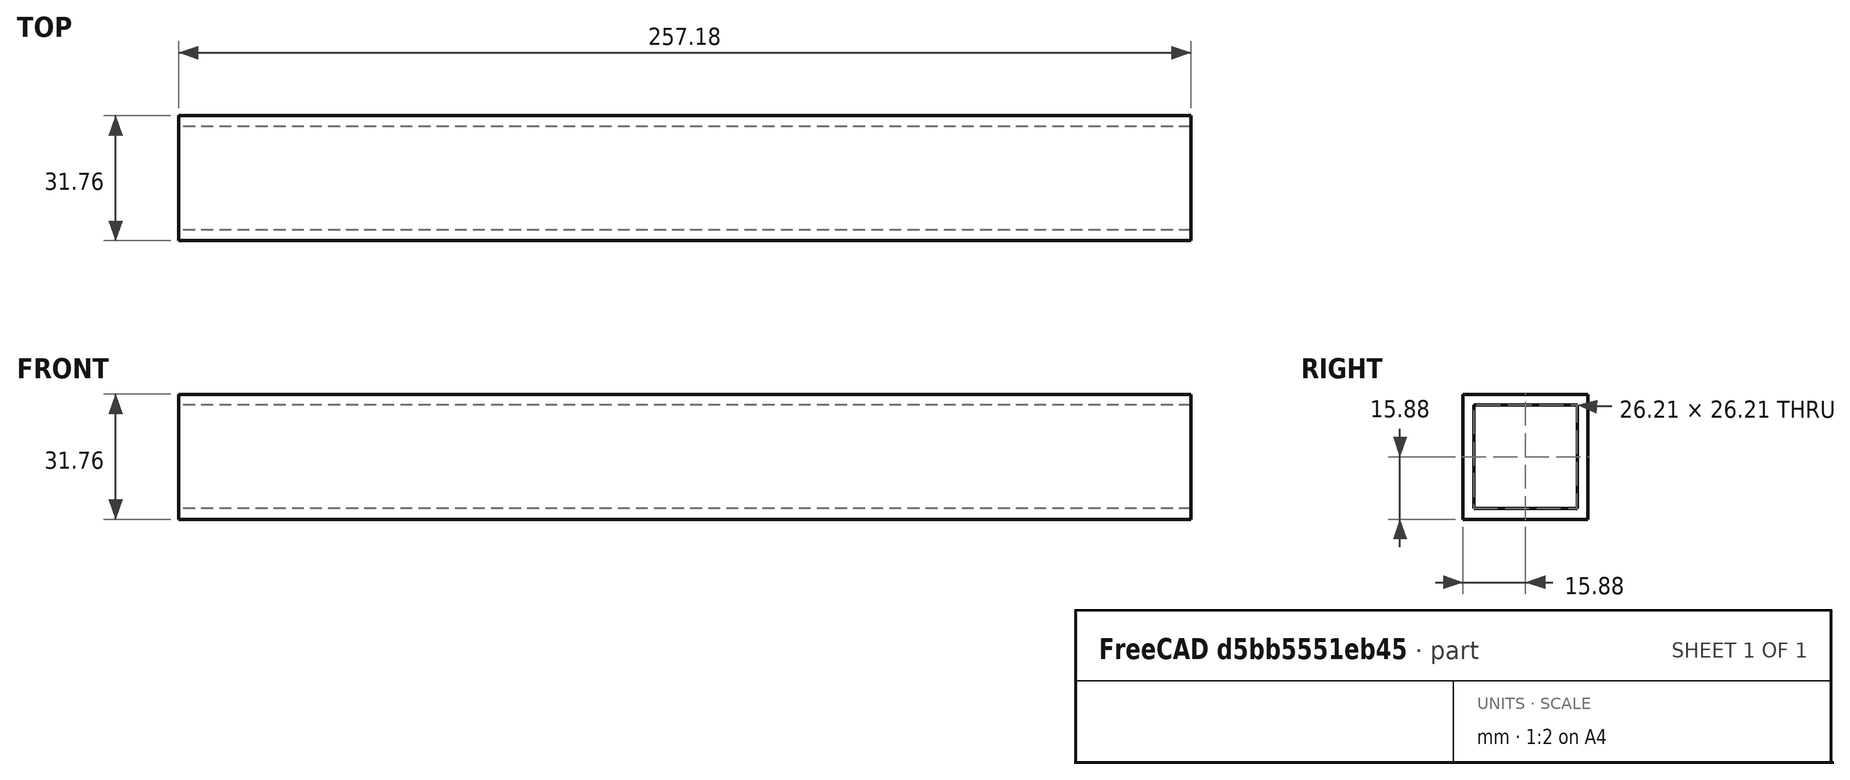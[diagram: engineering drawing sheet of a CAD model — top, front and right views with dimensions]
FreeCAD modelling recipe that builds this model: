
FCSTD DOCUMENT  (FreeCAD 0.16R6062 (Git))
Label: Chassis-Bottom-Part-7
License: All rights reserved
LicenseURL: http://en.wikipedia.org/wiki/All_rights_reserved
objects: Sketcher::SketchObject×1, PartDesign::Pad×1
note: 3 computed .brp shape members not serialized (recipe doc carries the construction recipe); baked Part::Feature solids carry a one-line shape summary decoded from their .brp

FEATURE [Sketcher::SketchObject] Sketch
  Placement = pos=(0,0,0) rot=(0.57735,0.57735,0.57735;2.0944rad)
  sketch-geometry (8):
    g0: LineSegment StartX=-15.875 StartY=15.875 StartZ=0 EndX=15.875 EndY=15.875 EndZ=0
    g1: LineSegment StartX=15.875 StartY=15.875 StartZ=0 EndX=15.875 EndY=-15.875 EndZ=0
    g2: LineSegment StartX=15.875 StartY=-15.875 StartZ=0 EndX=-15.875 EndY=-15.875 EndZ=0
    g3: LineSegment StartX=-15.875 StartY=-15.875 StartZ=0 EndX=-15.875 EndY=15.875 EndZ=0
    g4: LineSegment StartX=-13.1064 StartY=13.1064 StartZ=0 EndX=13.1064 EndY=13.1064 EndZ=0
    g5: LineSegment StartX=13.1064 StartY=13.1064 StartZ=0 EndX=13.1064 EndY=-13.1064 EndZ=0
    g6: LineSegment StartX=13.1064 StartY=-13.1064 StartZ=0 EndX=-13.1064 EndY=-13.1064 EndZ=0
    g7: LineSegment StartX=-13.1064 StartY=-13.1064 StartZ=0 EndX=-13.1064 EndY=13.1064 EndZ=0
  constraints (22):
    c: Coincident(g0,g1)
    c: Coincident(g1,g2)
    c: Coincident(g2,g3)
    c: Coincident(g3,g0)
    c: Horizontal(g0)
    c: Horizontal(g2)
    c: Vertical(g1)
    c: Vertical(g3)
    c: Equal(g2,g1)
    c: DistanceX(g0) = 31.75
    c: Symmetric(g0,g1,g-1)
    c: Coincident(g4,g5)
    c: Coincident(g5,g6)
    c: Coincident(g6,g7)
    c: Coincident(g7,g4)
    c: Horizontal(g4)
    c: Horizontal(g6)
    c: Vertical(g5)
    c: Vertical(g7)
    c: Equal(g6,g5)
    c: DistanceX(g4) = 26.2128
    c: Symmetric(g4,g5,g-1)
FEATURE [PartDesign::Pad] Pad
  Length = 257.175
  Length2 = 100
  Placement = pos=(0,0,0) rot=(0.57735,0.57735,0.57735;2.0944rad)
  Reversed = true
  Sketch = -> Sketch
  Type = 0
